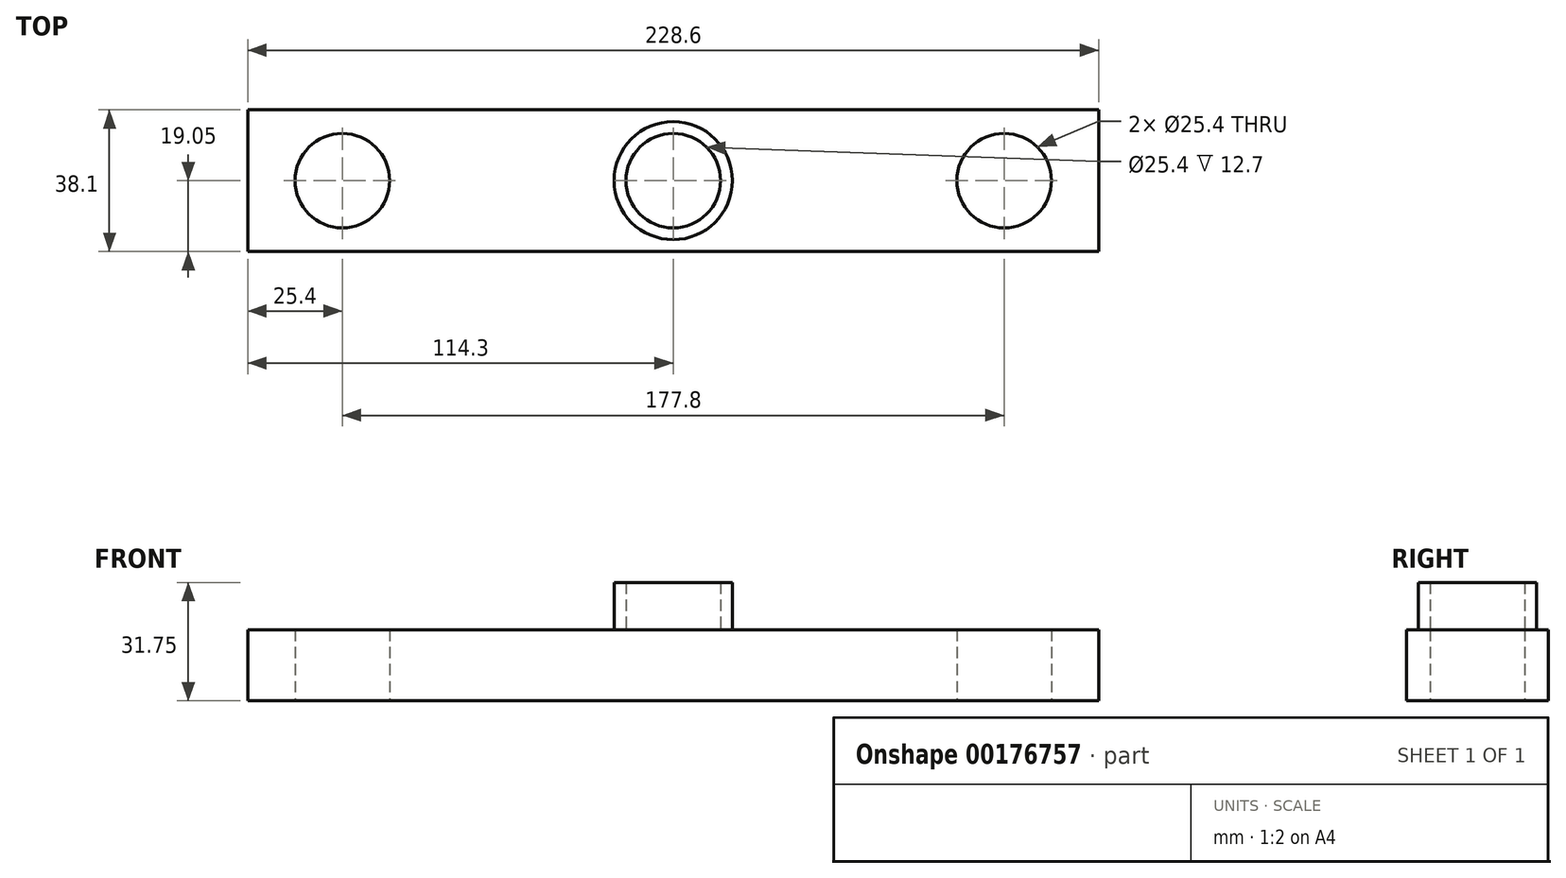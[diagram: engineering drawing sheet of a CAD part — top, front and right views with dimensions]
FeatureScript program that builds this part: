
annotation { "Feature Type Name" : "Feature", "Feature Type Description" : "" }
export const myFeature = defineFeature(function(context is Context, id is Id, definition is map)
    precondition{}
    {
        {
            var Q0;
            Q0=qCreatedBy(makeId("Top.planeOp"),FACE);
            var sketch = newSketch(context, id + "F0", { "sketchPlane" : qUnion([Q0])});
            skLineSegment(sketch, "E0.bottom", {"start": v(-114.3, 19.05) * mm, "end": v(114.3, 19.05) * mm});
            skLineSegment(sketch, "E0.top", {"start": v(-114.3, -19.05) * mm, "end": v(114.3, -19.05) * mm});
            skLineSegment(sketch, "E0.left", {"start": v(-114.3, 19.05) * mm, "end": v(-114.3, -19.05) * mm});
            skLineSegment(sketch, "E0.right", {"start": v(114.3, 19.05) * mm, "end": v(114.3, -19.05) * mm});
            skPoint(sketch, "E0.middle", {"position": v(0, 0) * mm});
            skCircle(sketch, "E1", {"center": v(-88.9, 0) * mm, "radius": 12.7 * mm});
            skCircle(sketch, "E2.MirrorC", {"center": v(88.9, 0) * mm, "radius": 12.7 * mm});
            skSolve(sketch);
        }
        {
            var Q0;
            Q0=makeQuery(id+"F0.imprint","IMPRINT",FACE,{"disambiguationData":[TD([[makeQuery(id+"F0.imprint","IMPRINT",EDGE,{"derivedFrom":sQuery(id+"F0.wireOp",EDGE,"E0.bottom")}),-1.0]])]});
            extrude(context, id + "F1", {"entities" : qUnion([Q0]), "depth" : 19.05 * mm});
        }
        {
            var Q0;
            Q0=makeQuery(id+"F1.opExtrude","CAP_FACE",FACE,{"disambiguationData":[OSD([sQuery(id+"F0.wireOp",EDGE,"E0.bottom"),sQuery(id+"F0.wireOp",EDGE,"E0.top"),sQuery(id+"F0.wireOp",EDGE,"E0.left"),sQuery(id+"F0.wireOp",EDGE,"E0.right"),sQuery(id+"F0.wireOp",EDGE,"E1"),sQuery(id+"F0.wireOp",EDGE,"E2.MirrorC")])],"isStart":false});
            var sketch = newSketch(context, id + "F2", { "sketchPlane" : qUnion([Q0])});
            skCircle(sketch, "E3", {"center": v(0, 0) * mm, "radius": 15.88 * mm});
            skCircle(sketch, "E4", {"center": v(0, 0) * mm, "radius": 12.7 * mm});
            skSolve(sketch);
        }
        {
            var Q0;
            Q0=makeQuery(id+"F2.imprint","IMPRINT",FACE,{"disambiguationData":[TD([[makeQuery(id+"F2.imprint","IMPRINT",EDGE,{"derivedFrom":sQuery(id+"F2.wireOp",EDGE,"E3")}),1.0]])]});
            extrude(context, id + "F3", {"entities" : qUnion([Q0]), "operationType" : NewBodyOperationType.ADD, "depth" : 12.7 * mm});
        }
    });
